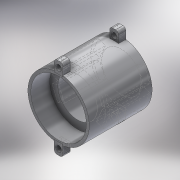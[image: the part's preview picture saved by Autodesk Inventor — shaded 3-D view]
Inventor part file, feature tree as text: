
AUTODESK INVENTOR PART (.ipt)
format: ipt  version: 2018 (Build 220112000, 112)  size: 236,032 bytes
history: native  units: in
note: dims shown in document units (in); Inventor stores cm internally (conversion verified against a paired STEP export)
features: move_body x7, direct_edit x3, fillet x1
ambient origin geometry x8: Origin, YZ Plane, XZ Plane, XY Plane, X Axis, Y Axis, Z Axis, Center Point
bodies: Solid1 (feature_tree)
feature tree (11):
  direct_edit  "Direct Edit1"
  direct_edit  "Direct Edit2"
  direct_edit  "Direct Edit3"
  fillet  "Fillet2"  [1 undecoded]
  move_body  "Move1"
  move_body  "Move2"
  move_body  "Move3"
  move_body  "Move4"
  move_body  "Move5"
  move_body  "Move6"
  move_body  "Move7"
note: 1 required parameter value undecoded (feature->parameter linkage not recoverable at this tier; creation-order binding heuristic only, values carry confidence <= 0.55)
